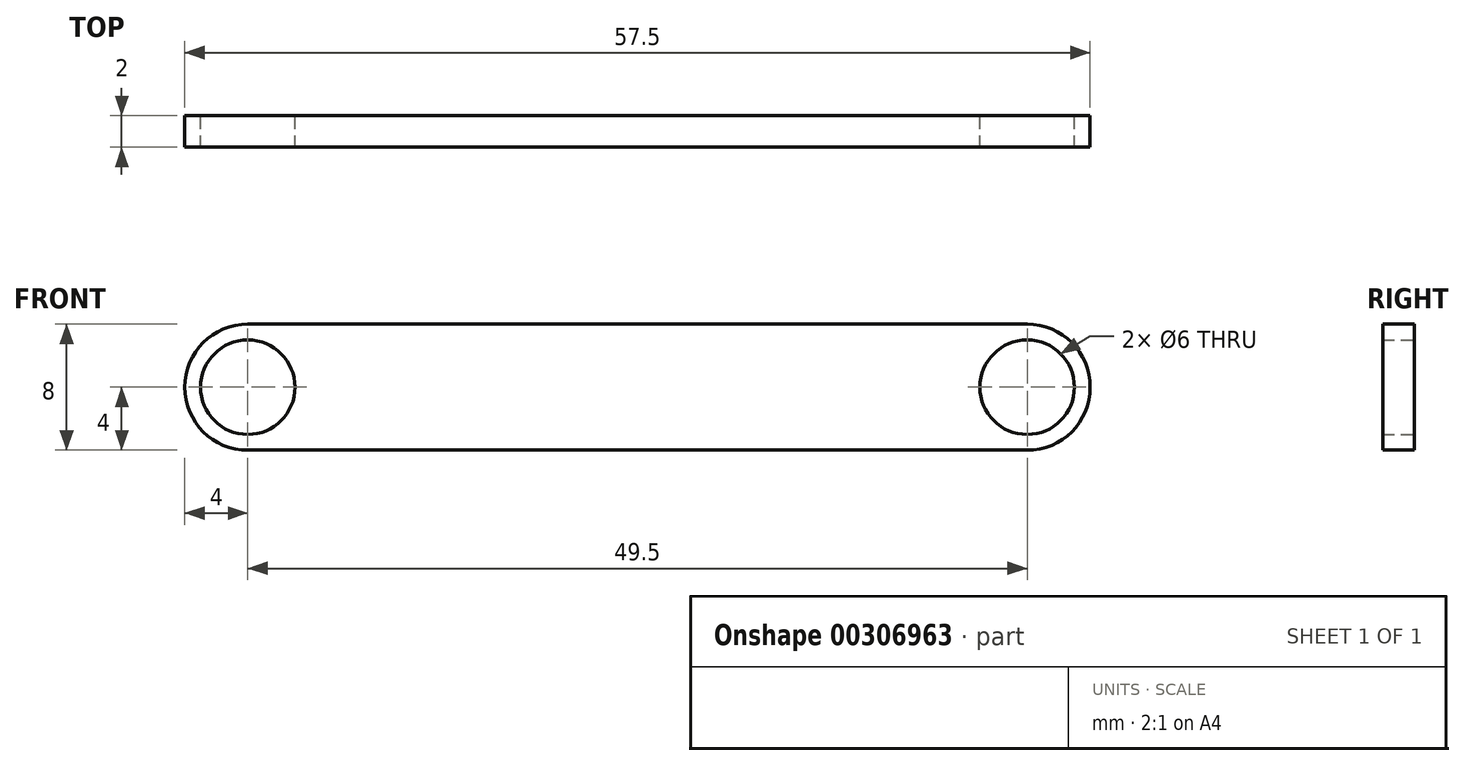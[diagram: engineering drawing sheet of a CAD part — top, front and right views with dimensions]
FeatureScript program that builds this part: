
annotation { "Feature Type Name" : "Feature", "Feature Type Description" : "" }
export const myFeature = defineFeature(function(context is Context, id is Id, definition is map)
    precondition{}
    {
        {
            var Q0;
            Q0=qCreatedBy(makeId("Front.planeOp"),FACE);
            var sketch = newSketch(context, id + "F0", { "sketchPlane" : qUnion([Q0])});
            skCircle(sketch, "E0", {"center": v(-24.75, 0) * mm, "radius": 3 * mm});
            skCircle(sketch, "E1", {"center": v(24.75, 0) * mm, "radius": 3 * mm});
            skArc(sketch, "E2", {"start": v(-24.75, 4) * mm, "mid": v(-28.75, 0) * mm, "end": v(-24.75, -4) * mm});
            skArc(sketch, "E3", {"start": v(24.75, -4) * mm, "mid": v(28.75, 0) * mm, "end": v(24.75, 4) * mm});
            skLineSegment(sketch, "E4", {"start": v(-24.75, 4) * mm, "end": v(24.75, 4) * mm});
            skLineSegment(sketch, "E5", {"start": v(-24.75, -4) * mm, "end": v(24.75, -4) * mm});
            skSolve(sketch);
        }
        {
            var Q0;
            Q0 = qSketchRegion(id + "F0", true);
            extrude(context, id + "F1", {"entities" : qUnion([Q0]), "depth" : 2 * mm});
        }
    });
